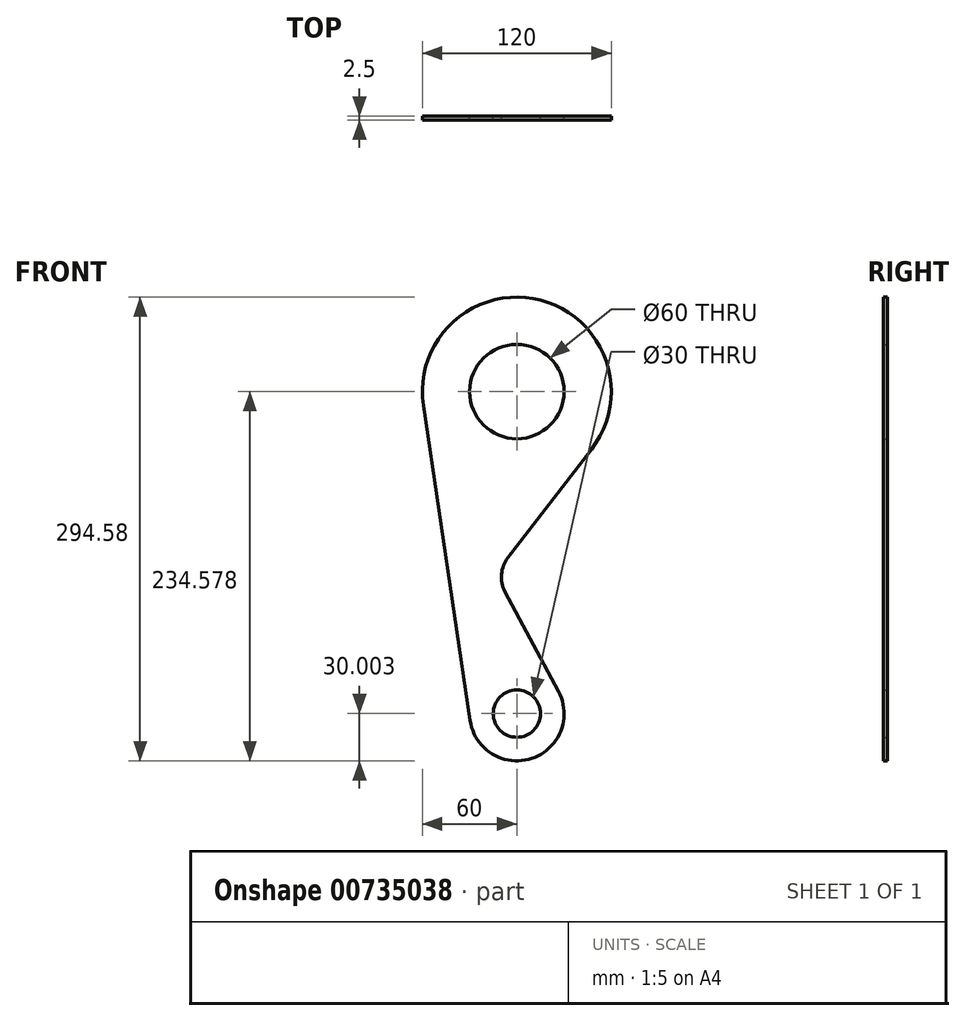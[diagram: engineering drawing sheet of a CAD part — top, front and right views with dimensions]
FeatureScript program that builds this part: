
annotation { "Feature Type Name" : "Feature", "Feature Type Description" : "" }
export const myFeature = defineFeature(function(context is Context, id is Id, definition is map)
    precondition{}
    {
        {
            var Q0;
            Q0=qCreatedBy(makeId("Front.planeOp"),FACE);
            var sketch = newSketch(context, id + "F0", { "sketchPlane" : qUnion([Q0])});
            skLineSegment(sketch, "E0.bottom", {"start": v(-114.58, -150.55) * mm, "end": v(185.42, -150.55) * mm, "construction": true});
            skLineSegment(sketch, "E0.top", {"start": v(-114.58, 149.45) * mm, "end": v(185.42, 149.45) * mm, "construction": true});
            skLineSegment(sketch, "E0.left", {"start": v(-114.58, -150.55) * mm, "end": v(-114.58, 149.45) * mm, "construction": true});
            skLineSegment(sketch, "E0.right", {"start": v(185.42, -150.55) * mm, "end": v(185.42, 149.45) * mm, "construction": true});
            skArc(sketch, "E1", {"start": v(-2.89, -124.03) * mm, "mid": v(36.2, -148.1) * mm, "end": v(53.24, -105.47) * mm});
            skLineSegment(sketch, "E2", {"start": v(26.79, 84.95) * mm, "end": v(26.79, -119.63) * mm, "construction": true});
            skArc(sketch, "E3", {"start": v(74.28, 48.28) * mm, "mid": v(41.94, 143) * mm, "end": v(-32.56, 76.15) * mm});
            skLineSegment(sketch, "E4", {"start": v(-32.56, 76.15) * mm, "end": v(-2.89, -124.03) * mm});
            skArc(sketch, "E5", {"start": v(21.15, -20.52) * mm, "mid": v(17.05, -31.09) * mm, "end": v(19.35, -42.18) * mm});
            skLineSegment(sketch, "E6", {"start": v(19.35, -42.18) * mm, "end": v(53.24, -105.47) * mm});
            skLineSegment(sketch, "E7", {"start": v(74.28, 48.28) * mm, "end": v(21.15, -20.52) * mm});
            skPoint(sketch, "E8.orphan", {"position": v(0, -6.04) * mm});
            skCircle(sketch, "E9", {"center": v(26.79, 84.95) * mm, "radius": 30 * mm});
            skCircle(sketch, "E10", {"center": v(26.79, -119.63) * mm, "radius": 15 * mm});
            skSolve(sketch);
        }
        {
            var Q0;
            Q0 = qSketchRegion(id + "F0", true);
            extrude(context, id + "F1", {"entities" : qUnion([Q0]), "depth" : 2.5 * mm, "offsetDistance" : 25 * mm});
        }
    });
